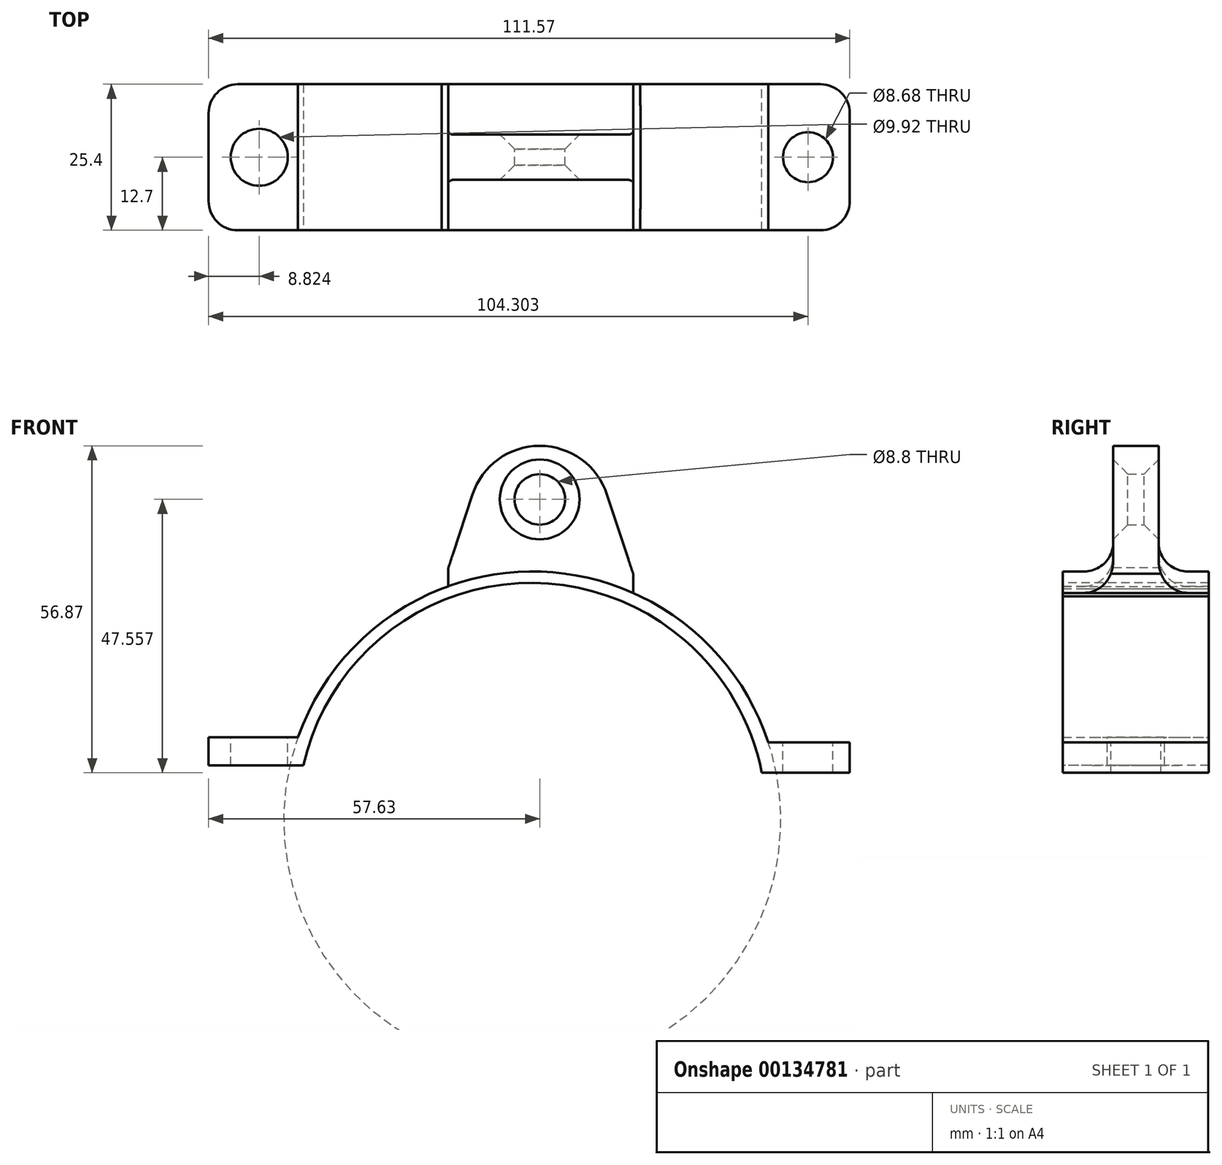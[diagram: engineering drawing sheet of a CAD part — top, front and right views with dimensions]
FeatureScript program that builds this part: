
annotation { "Feature Type Name" : "Feature", "Feature Type Description" : "" }
export const myFeature = defineFeature(function(context is Context, id is Id, definition is map)
    precondition{}
    {
        {
            var Q0;
            Q0=qCreatedBy(makeId("Front.planeOp"),FACE);
            var sketch = newSketch(context, id + "F0", { "sketchPlane" : qUnion([Q0])});
            skLineSegment(sketch, "E0", {"start": v(-17.6, 9.08) * mm, "end": v(-11.73, 26.95) * mm});
            skLineSegment(sketch, "E1.MirrorCS", {"start": v(17.6, 9.08) * mm, "end": v(11.73, 26.95) * mm});
            skArc(sketch, "E2", {"start": v(11.73, 26.95) * mm, "mid": v(0, 35.45) * mm, "end": v(-11.73, 26.95) * mm});
            skArc(sketch, "E3", {"start": v(17.6, 9.08) * mm, "mid": v(0, 11.67) * mm, "end": v(-17.6, 9.08) * mm});
            skSolve(sketch);
        }
        {
            var Q0;
            Q0 = qSketchRegion(id + "F0", true);
            extrude(context, id + "F1", {"entities" : qUnion([Q0]), "endBound" : BoundingType.SYMMETRIC, "depth" : 7.89 * mm});
        }
        {
            var Q0;
            Q0=qCreatedBy(makeId("Front.planeOp"),FACE);
            var sketch = newSketch(context, id + "F2", { "sketchPlane" : qUnion([Q0])});
            skArc(sketch, "E4", {"start": v(39.94, -16.62) * mm, "mid": v(-0.71, 13.59) * mm, "end": v(-42.17, -15.5) * mm});
            skArc(sketch, "E5", {"start": v(36.3, -16.62) * mm, "mid": v(-1.1, 10.3) * mm, "end": v(-39.1, -15.78) * mm});
            skLineSegment(sketch, "E6", {"start": v(-42.17, -15.5) * mm, "end": v(-39.1, -15.78) * mm});
            skLineSegment(sketch, "E7", {"start": v(36.3, -16.62) * mm, "end": v(39.94, -16.62) * mm});
            skSolve(sketch);
        }
        {
            var Q0;
            Q0 = qSketchRegion(id + "F2", true);
            extrude(context, id + "F3", {"entities" : qUnion([Q0]), "operationType" : NewBodyOperationType.ADD, "endBound" : BoundingType.SYMMETRIC, "depth" : 25.4 * mm});
        }
        {
            var Q0;
            Q0=makeQuery(id+"F3.boolean.opBoolean","INTERSECT",EDGE,{"derivedFrom":[makeQuery(id+"F1.opExtrude","CAP_FACE",FACE,{"disambiguationData":[OSD([sQuery(id+"F0.wireOp",EDGE,"E0"),sQuery(id+"F0.wireOp",EDGE,"E1.MirrorCS"),sQuery(id+"F0.wireOp",EDGE,"E2"),sQuery(id+"F0.wireOp",EDGE,"E3")])],"isStart":false}),makeQuery(id+"F3.opExtrude","SWEPT_FACE",FACE,{"disambiguationData":[OSD([sQuery(id+"F2.wireOp",EDGE,"E4")])]})]});
            var Q1;
            Q1=makeQuery(id+"F3.boolean.opBoolean","INTERSECT",EDGE,{"derivedFrom":[makeQuery(id+"F1.opExtrude","CAP_FACE",FACE,{"disambiguationData":[OSD([sQuery(id+"F0.wireOp",EDGE,"E0"),sQuery(id+"F0.wireOp",EDGE,"E1.MirrorCS"),sQuery(id+"F0.wireOp",EDGE,"E2"),sQuery(id+"F0.wireOp",EDGE,"E3")])],"isStart":true}),makeQuery(id+"F3.opExtrude","SWEPT_FACE",FACE,{"disambiguationData":[OSD([sQuery(id+"F2.wireOp",EDGE,"E4")])]})]});
            fillet(context, id + "F4", {"entities" : qUnion([Q0, Q1]), "radius" : 5.08 * mm, "tangentPropagation" : true, "allowEdgeOverflow" : false});
        }
        {
            var Q0;
            Q0=qCreatedBy(makeId("Front.planeOp"),FACE);
            var sketch = newSketch(context, id + "F5", { "sketchPlane" : qUnion([Q0])});
            skLineSegment(sketch, "E8", {"start": v(-39.66, -15.2) * mm, "end": v(-57.63, -15.2) * mm});
            skLineSegment(sketch, "E9", {"start": v(-57.63, -15.2) * mm, "end": v(-57.63, -20.12) * mm});
            skLineSegment(sketch, "E10", {"start": v(-57.63, -20.12) * mm, "end": v(-39.85, -20.12) * mm});
            skLineSegment(sketch, "E11", {"start": v(-39.85, -20.12) * mm, "end": v(-39.66, -15.2) * mm});
            skSolve(sketch);
        }
        {
            var Q0;
            Q0 = qSketchRegion(id + "F5", true);
            extrude(context, id + "F6", {"entities" : qUnion([Q0]), "operationType" : NewBodyOperationType.ADD, "endBound" : BoundingType.SYMMETRIC, "depth" : 25.4 * mm});
        }
        {
            var Q0;
            Q0=qCreatedBy(makeId("Front.planeOp"),FACE);
            var sketch = newSketch(context, id + "F7", { "sketchPlane" : qUnion([Q0])});
            skLineSegment(sketch, "E12", {"start": v(36.16, -16.1) * mm, "end": v(53.94, -16.1) * mm});
            skLineSegment(sketch, "E13", {"start": v(53.94, -16.1) * mm, "end": v(53.94, -21.42) * mm});
            skLineSegment(sketch, "E14", {"start": v(53.94, -21.42) * mm, "end": v(36.16, -21.42) * mm});
            skLineSegment(sketch, "E15", {"start": v(36.16, -16.1) * mm, "end": v(36.16, -21.42) * mm});
            skSolve(sketch);
        }
        {
            var Q0;
            Q0 = qSketchRegion(id + "F7", true);
            extrude(context, id + "F8", {"entities" : qUnion([Q0]), "operationType" : NewBodyOperationType.ADD, "endBound" : BoundingType.SYMMETRIC, "depth" : 25.4 * mm});
        }
        {
            var Q0;
            Q0 = qSketchRegion(id + "F5", true);
            extrude(context, id + "F9", {"entities" : qUnion([Q0]), "operationType" : NewBodyOperationType.ADD, "depth" : 8.67 * mm});
        }
        {
            var Q0;
            Q0 = qSketchRegion(id + "F7", true);
            extrude(context, id + "F10", {"entities" : qUnion([Q0]), "operationType" : NewBodyOperationType.ADD, "depth" : 9.47 * mm});
        }
        {
            var Q0;
            Q0=qCreatedBy(makeId("Front.planeOp"),FACE);
            var sketch = newSketch(context, id + "F11", { "sketchPlane" : qUnion([Q0])});
            skArc(sketch, "E16", {"start": v(38.67, -21.6) * mm, "mid": v(-0.42, 11.4) * mm, "end": v(-40.8, -20) * mm});
            skArc(sketch, "E17", {"start": v(-40.8, -20) * mm, "mid": v(-1.74, -54.24) * mm, "end": v(38.67, -21.6) * mm});
            skSolve(sketch);
        }
        {
            var Q0;
            Q0 = qSketchRegion(id + "F11", true);
            extrude(context, id + "F12", {"entities" : qUnion([Q0]), "operationType" : NewBodyOperationType.REMOVE, "endBound" : BoundingType.SYMMETRIC, "depth" : 25.4 * mm});
        }
        {
            var Q0;
            Q0 = qSketchRegion(id + "F11", true);
            extrude(context, id + "F13", {"entities" : qUnion([Q0]), "operationType" : NewBodyOperationType.REMOVE, "endBound" : BoundingType.SYMMETRIC, "depth" : 25.4 * mm});
        }
        {
            var Q0;
            Q0=makeQuery(id+"F1.opExtrude","CAP_FACE",FACE,{"disambiguationData":[OSD([sQuery(id+"F0.wireOp",EDGE,"E0"),sQuery(id+"F0.wireOp",EDGE,"E1.MirrorCS"),sQuery(id+"F0.wireOp",EDGE,"E2"),sQuery(id+"F0.wireOp",EDGE,"E3")])],"isStart":false});
            var sketch = newSketch(context, id + "F14", { "sketchPlane" : qUnion([Q0])});
            skCircle(sketch, "E18", {"center": v(0, 26.14) * mm, "radius": 4.4 * mm});
            skSolve(sketch);
        }
        {
            var Q0;
            Q0 = qSketchRegion(id + "F14", true);
            extrude(context, id + "F15", {"entities" : qUnion([Q0]), "operationType" : NewBodyOperationType.REMOVE, "endBound" : BoundingType.SYMMETRIC, "depth" : 107.46 * mm});
        }
        {
            var Q0;
            Q0=makeQuery(id+"F15.boolean.opBoolean","INTERSECT",EDGE,{"derivedFrom":[makeQuery(id+"F1.opExtrude","CAP_FACE",FACE,{"disambiguationData":[OSD([sQuery(id+"F0.wireOp",EDGE,"E0"),sQuery(id+"F0.wireOp",EDGE,"E1.MirrorCS"),sQuery(id+"F0.wireOp",EDGE,"E2"),sQuery(id+"F0.wireOp",EDGE,"E3")])],"isStart":false}),makeQuery(id+"F15.opExtrude","SWEPT_FACE",FACE,{"disambiguationData":[OSD([sQuery(id+"F14.wireOp",EDGE,"E18")])]})]});
            chamfer(context, id + "F16", {"entities" : qUnion([Q0]), "width" : 2.54 * mm, "tangentPropagation" : true});
        }
        {
            var Q0;
            Q0=makeQuery(id+"F15.boolean.opBoolean","INTERSECT",EDGE,{"derivedFrom":[makeQuery(id+"F1.opExtrude","CAP_FACE",FACE,{"disambiguationData":[OSD([sQuery(id+"F0.wireOp",EDGE,"E0"),sQuery(id+"F0.wireOp",EDGE,"E1.MirrorCS"),sQuery(id+"F0.wireOp",EDGE,"E2"),sQuery(id+"F0.wireOp",EDGE,"E3")])],"isStart":true}),makeQuery(id+"F15.opExtrude","SWEPT_FACE",FACE,{"disambiguationData":[OSD([sQuery(id+"F14.wireOp",EDGE,"E18")])]})]});
            chamfer(context, id + "F17", {"entities" : qUnion([Q0]), "width" : 2.54 * mm, "tangentPropagation" : true});
        }
        {
            var Q0;
            Q0=makeQuery(id+"F8.opExtrude","CAP_EDGE",EDGE,{"disambiguationData":[OSD([sQuery(id+"F7.wireOp",EDGE,"E13")])],"isStart":true});
            var Q1;
            Q1=makeQuery(id+"F8.opExtrude","CAP_EDGE",EDGE,{"disambiguationData":[OSD([sQuery(id+"F7.wireOp",EDGE,"E13")])],"isStart":false});
            var Q2;
            Q2=makeQuery(id+"F6.opExtrude","CAP_EDGE",EDGE,{"disambiguationData":[OSD([sQuery(id+"F5.wireOp",EDGE,"E9")])],"isStart":true});
            var Q3;
            Q3=makeQuery(id+"F6.opExtrude","CAP_EDGE",EDGE,{"disambiguationData":[OSD([sQuery(id+"F5.wireOp",EDGE,"E9")])],"isStart":false});
            fillet(context, id + "F18", {"entities" : qUnion([Q0, Q1, Q2, Q3]), "radius" : 5.08 * mm, "tangentPropagation" : true, "allowEdgeOverflow" : false});
        }
        {
            var Q0;
            Q0=makeQuery(id+"F6.opExtrude","SWEPT_FACE",FACE,{"disambiguationData":[OSD([sQuery(id+"F5.wireOp",EDGE,"E8")])]});
            var sketch = newSketch(context, id + "F19", { "sketchPlane" : qUnion([Q0])});
            skCircle(sketch, "E19", {"center": v(-48.8, 0) * mm, "radius": 4.96 * mm});
            skCircle(sketch, "E20", {"center": v(46.67, 0) * mm, "radius": 4.34 * mm});
            skSolve(sketch);
        }
        {
            var Q0;
            Q0 = qSketchRegion(id + "F19", true);
            extrude(context, id + "F20", {"entities" : qUnion([Q0]), "operationType" : NewBodyOperationType.REMOVE, "oppositeDirection" : true, "depth" : 23.49 * mm});
        }
        {
            var Q0;
            Q0=qCreatedBy(makeId("Front.planeOp"),FACE);
            var sketch = newSketch(context, id + "F21", { "sketchPlane" : qUnion([Q0])});
            skArc(sketch, "E21", {"start": v(39.04, -25.94) * mm, "mid": v(-0.46, 11.6) * mm, "end": v(-41.8, -23.92) * mm});
            skLineSegment(sketch, "E22", {"start": v(-41.8, -23.92) * mm, "end": v(39.04, -25.94) * mm});
            skSolve(sketch);
        }
        {
            var Q0;
            Q0 = qSketchRegion(id + "F21", true);
            extrude(context, id + "F22", {"entities" : qUnion([Q0]), "operationType" : NewBodyOperationType.REMOVE, "endBound" : BoundingType.SYMMETRIC, "oppositeDirection" : true, "depth" : 36.42 * mm});
        }
        {
            var Q0;
            Q0=qCreatedBy(makeId("Front.planeOp"),FACE);
            var sketch = newSketch(context, id + "F23", { "sketchPlane" : qUnion([Q0])});
            skLineSegment(sketch, "E23", {"start": v(-15.9, 11.02) * mm, "end": v(-15.9, 14.88) * mm});
            skLineSegment(sketch, "E24", {"start": v(-15.9, 14.88) * mm, "end": v(-17.1, 10.6) * mm});
            skLineSegment(sketch, "E25", {"start": v(-17.1, 10.6) * mm, "end": v(-15.9, 11.02) * mm});
            skSolve(sketch);
        }
        {
            var Q0;
            Q0 = qSketchRegion(id + "F23", true);
            extrude(context, id + "F24", {"entities" : qUnion([Q0]), "operationType" : NewBodyOperationType.REMOVE, "endBound" : BoundingType.SYMMETRIC, "depth" : 25.4 * mm});
        }
        {
            var Q0;
            Q0=qCreatedBy(makeId("Front.planeOp"),FACE);
            var sketch = newSketch(context, id + "F25", { "sketchPlane" : qUnion([Q0])});
            skLineSegment(sketch, "E26", {"start": v(16.24, 13.56) * mm, "end": v(16.24, 9.86) * mm});
            skLineSegment(sketch, "E27", {"start": v(16.24, 9.86) * mm, "end": v(17.6, 9.25) * mm});
            skLineSegment(sketch, "E28", {"start": v(17.6, 9.25) * mm, "end": v(16.24, 13.56) * mm});
            skSolve(sketch);
        }
        {
            var Q0;
            Q0 = qSketchRegion(id + "F25", true);
            extrude(context, id + "F26", {"entities" : qUnion([Q0]), "operationType" : NewBodyOperationType.REMOVE, "endBound" : BoundingType.SYMMETRIC, "depth" : 40.27 * mm});
        }
    });
